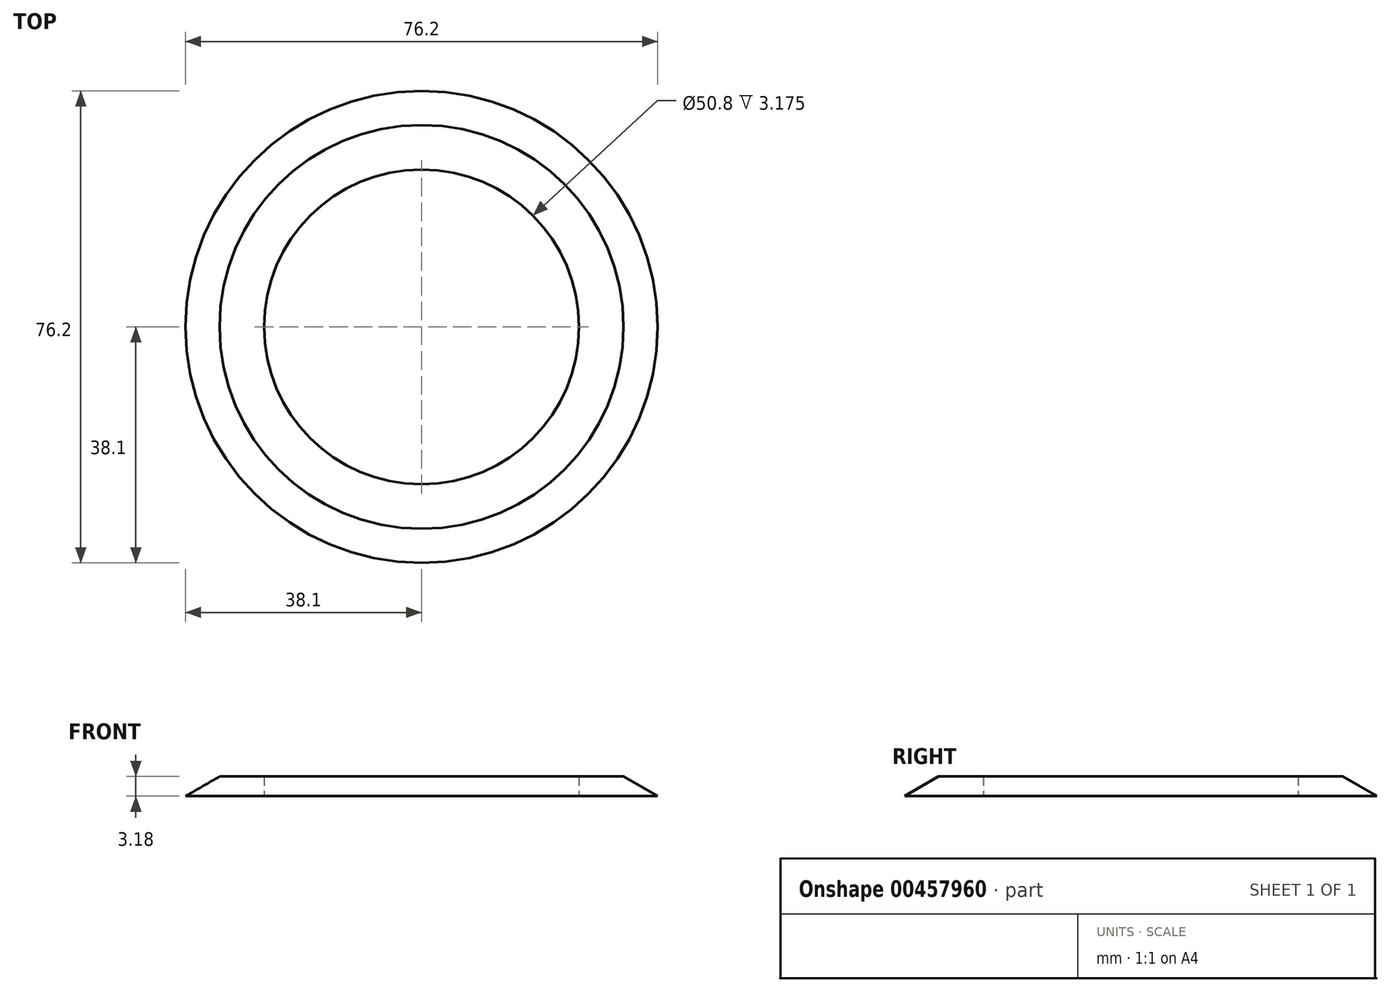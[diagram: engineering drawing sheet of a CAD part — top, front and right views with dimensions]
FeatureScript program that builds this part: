
annotation { "Feature Type Name" : "Feature", "Feature Type Description" : "" }
export const myFeature = defineFeature(function(context is Context, id is Id, definition is map)
    precondition{}
    {
        {
            var Q0;
            Q0=qCreatedBy(makeId("Front.planeOp"),FACE);
            var sketch = newSketch(context, id + "F0", { "sketchPlane" : qUnion([Q0])});
            skLineSegment(sketch, "E0", {"start": v(0, 0) * mm, "end": v(0, 29.1) * mm, "construction": true});
            skLineSegment(sketch, "E1", {"start": v(-25.4, 0) * mm, "end": v(-38.1, 0) * mm});
            skLineSegment(sketch, "E2", {"start": v(-38.1, 0) * mm, "end": v(-32.6, 3.17) * mm});
            skLineSegment(sketch, "E3", {"start": v(-32.6, 3.17) * mm, "end": v(-25.4, 3.17) * mm});
            skLineSegment(sketch, "E4", {"start": v(-25.4, 3.17) * mm, "end": v(-25.4, 0) * mm});
            skSolve(sketch);
        }
        {
            var Q0;
            Q0=qSketchRegion(id+"F0",true);
            var Q1;
            Q1=sQuery(id+"F0.wireOp",EDGE,"E0");
            revolve(context, id + "F1", {"entities" : qUnion([Q0]), "axis" : qUnion([Q1]), "revolveType" : RevolveType.FULL});
        }
    });
